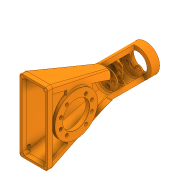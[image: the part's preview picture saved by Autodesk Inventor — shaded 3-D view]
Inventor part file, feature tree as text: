
AUTODESK INVENTOR PART (.ipt)
format: ipt  version: 2020 (Build 240168000, 168)  size: 1,710,080 bytes
history: native  units: in
note: dims shown in document units (in); Inventor stores cm internally (conversion verified against a paired STEP export)
features: sketch x35, extrude x32, projected_geometry x23, chamfer x5, fillet x5, plane x4, loft x2, other x1
ambient origin geometry x8: Origin, YZ Plane, XZ Plane, XY Plane, X Axis, Y Axis, Z Axis, Center Point
bodies: Solid1 (feature_tree)
feature tree (107):
  extrude  "Extrusion1"  Depth=2.0472in
  extrude  "Extrusion2"  Depth=0.5591in
  chamfer  "Chamfer1"  Distance=0.5512in
  extrude  "Extrusion3"  Depth=0.5591in
  extrude  "Extrusion4"  Depth=0.2756in TaperAngle=0.0deg
  extrude  "Extrusion5"  Depth=0.315in
  extrude  "Extrusion6"  Depth=0.4724in
  extrude  "Extrusion7"  Depth=0.0787in
  plane  "Work Plane1"
  sketch  "Sketch9"  dims[d26=0.0984in d27=0.0in d28=0.1575in]
  plane  "Work Plane2"
  extrude  "Extrusion9"  Depth=0.1575in
  sketch  "Sketch11"  dims[d31=15.0deg d32=0.4921in d33=0.0in]
  plane  "Work Plane3"
  extrude  "Extrusion10"  Depth=0.1575in
  extrude  "Extrusion11"  Depth=0.4921in TaperAngle=0.0deg
  loft  "Loft1"
  loft  "Loft2"
  sketch  "Sketch16"  dims[d47=0.315in d48=0.4331in]
  extrude  "Extrusion12"  Depth=0.0787in
  extrude  "Extrusion13"  Depth=0.0984in TaperAngle=0.0deg
  extrude  "Extrusion14"  Depth=0.4331in
  extrude  "Extrusion15"  Depth=0.1575in
  chamfer  "Chamfer23"  Distance=0.0984in
  extrude  "Extrusion19"  Depth=0.8858in
  extrude  "Extrusion20"  Depth=1.6654in
  extrude  "Extrusion21"  TaperAngle=0.0deg  [1 undecoded]
  extrude  "Extrusion22"  Depth=1.6654in
  extrude  "Extrusion23"  Depth=0.1969in
  extrude  "Extrusion24"  Depth=0.3484in
  extrude  "Extrusion25"  Depth=0.1969in
  chamfer  "Chamfer24"  Distance=0.3937in
  extrude  "Extrusion26"  TaperAngle=0.0deg  [1 undecoded]
  fillet  "Fillet2"  [1 undecoded]
  extrude  "Extrusion27"  TaperAngle=0.0deg  [1 undecoded]
  extrude  "Extrusion28"  Depth=0.3937in
  fillet  "Fillet4"  Radius=0.3937in
  fillet  "Fillet5"  Radius=0.7874in
  extrude  "Extrusion29"  Depth=0.8858in
  fillet  "Fillet6"  Radius=1.6654in
  extrude  "Extrusion30"  TaperAngle=0.0deg  [1 undecoded]
  extrude  "Extrusion31"  Depth=0.2224in
  chamfer  "Chamfer26"  Distance=0.0984in
  extrude  "Extrusion32"  Depth=0.0984in
  extrude  "Extrusion33"  Depth=0.0984in TaperAngle=0.0deg
  extrude  "Extrusion34"  Depth=0.0984in
  plane  "Work Plane6"
  extrude  "Extrusion35"  Depth=0.3937in TaperAngle=45.0deg
  extrude  "Extrusion36"  Depth=0.0984in
  chamfer  "Chamfer27"  Distance=0.1969in
  fillet  "Fillet7"  Radius=0.2756in
  sketch  "Sketch1"  dims[d0=2.3622in d1=2.0472in]
  sketch  "Sketch2"  dims[d2=0.5591in d3=0.0in d4=1.6535in d5=0.5512in d6=0.0in]
  sketch  "Sketch3"  dims[d7=0.5591in d8=0.125in d9=0.0137in d10=0.0157in]
  sketch  "Sketch5"  dims[d11=4.7244in d13=360.0deg d15=0.2756in d16=0.0in]
  sketch  "Sketch6"  dims[d17=0.5512in d19=0.315in]
  projected_geometry  "Projected Loop1"
  sketch  "Sketch7"  dims[d20=0.315in d21=0.4724in]
  projected_geometry  "Projected Loop2"
  sketch  "Sketch8"  dims[d22=0.4724in d23=0.0787in d24=0.0787in d25=0.0787in]
  projected_geometry  "Projected Loop3"
  sketch  "Sketch10"  dims[d29=0.1575in d30=1.0994in]
  sketch  "Sketch12"  dims[d34=1.4567in d35=0.0in d36=1.5748in d38=360.0deg]
  sketch  "Sketch13"  dims[d40=0.0787in d41=0.0787in]
  projected_geometry  "Projected Loop4"
  other  "Edges1"
  sketch  "Sketch14"  dims[d42=0.0787in d43=0.0787in]
  projected_geometry  "Projected Loop5"
  sketch  "Sketch15"  dims[d44=0.0787in d45=0.0984in d46=0.0in]
  projected_geometry  "Projected Loop6"
  projected_geometry  "Projected Loop7"
  sketch  "Sketch19"  dims[d51=0.5374in d52=0.1575in]
  projected_geometry  "Projected Loop8"
  sketch  "Sketch20"  dims[d53=0.1575in d54=0.0984in d55=0.0in]
  projected_geometry  "Projected Loop9"
  sketch  "Sketch21"  dims[d56=6.6929in d57=0.8858in]
  sketch  "Sketch25"  dims[d58=1.6654in d59=1.6654in]
  sketch  "Sketch26"  dims[d60=0.0in d61=0.0in]
  projected_geometry  "Projected Loop11"
  sketch  "Sketch27"  dims[d62=1.6654in d63=1.6654in]
  projected_geometry  "Projected Loop12"
  sketch  "Sketch28"  dims[d64=0.1969in d65=0.1969in]
  sketch  "Sketch29"  dims[d66=0.3484in d67=0.3484in]
  sketch  "Sketch30"  dims[d68=0.1969in d69=0.1969in]
  sketch  "Sketch31"  dims[d70=0.1969in d71=0.3937in d72=0.0in]
  projected_geometry  "Projected Loop13"
  projected_geometry  "Projected Loop14"
  sketch  "Sketch33"  dims[d73=0.7874in d74=0.0in d75=0.0in d76=90.0deg d77=0.0in d78=90.0deg]
  projected_geometry  "Projected Loop15"
  sketch  "Sketch34"  dims[d79=0.0in d80=90.0deg d81=0.0in d82=90.0deg]
  sketch  "Sketch35"  dims[d86=0.7874in d87=0.0in d90=0.3937in d91=0.3937in d92=0.7874in d93=0.0in]
  projected_geometry  "Projected Loop16"
  projected_geometry  "Projected Loop17"
  sketch  "Sketch36"  dims[d94=0.1969in d95=0.0in d96=0.8858in d97=1.6654in]
  projected_geometry  "Projected Loop18"
  sketch  "Sketch37"  dims[d98=1.6654in d99=0.0in]
  projected_geometry  "Projected Loop19"
  sketch  "Sketch38"  dims[d100=0.0in d101=0.2224in]
  projected_geometry  "Projected Loop20"
  projected_geometry  "Projected Loop21"
  sketch  "Sketch39"  dims[d102=0.1575in]
  projected_geometry  "Projected Loop22"
  sketch  "Sketch40"  dims[d103=0.1575in]
  sketch  "Sketch41"  dims[d104=0.1575in]
  projected_geometry  "Projected Loop24"
  sketch  "Sketch42"  dims[d105=0.1575in d106=0.0984in d107=0.0984in d108=0.1969in d109=0.0in d193=0.0984in d194=0.3937in d195=0.125in d196=45.0deg d197=0.2756in d198=0.1969in d199=0.0in d200=0.2756in d201=2.7559in d202=0.2756in d203=0.2756in d204=0.2756in d205=0.2756in d206=0.2756in d207=0.2756in d208=0.2756in d209=0.0394in d210=0.2047in d211=0.0in d212=0.1969in d213=0.2756in d214=0.0in d215=1.0in d216=0.0in d217=0.2362in d218=0.2362in d219=0.2362in d220=0.2362in d221=0.2362in d222=0.0in d223=0.3937in d224=0.0in d225=0.1575in d226=0.0in d227=0.315in d228=0.187in d229=0.125in d230=45.0deg d231=1.0in d232=0.0in d233=0.1969in d235=0.4724in d236=0.0984in d237=0.0in d241=0.4724in d243=0.4724in d244=0.4331in d245=0.4724in d247=0.1181in d248=0.0984in d249=0.0in d250=0.0315in d251=0.0394in d252=1.0in d253=0.0in d254=0.315in d255=0.0787in d256=0.0in d257=0.0787in d258=0.0in d259=0.0315in d260=0.0984in d261=0.125in d262=45.0deg d263=0.1181in d264=0.0in d265=0.1181in d266=0.0in d267=0.0394in d268=0.0in d269=0.4528in d270=0.0984in d271=0.0in d272=0.0984in d273=0.0in d274=0.0984in d275=0.125in d276=45.0deg d238=0.5in d239=0.0344in]
  projected_geometry  "Projected Loop25"
note: 5 required parameter values undecoded (feature->parameter linkage not recoverable at this tier; creation-order binding heuristic only, values carry confidence <= 0.55)
